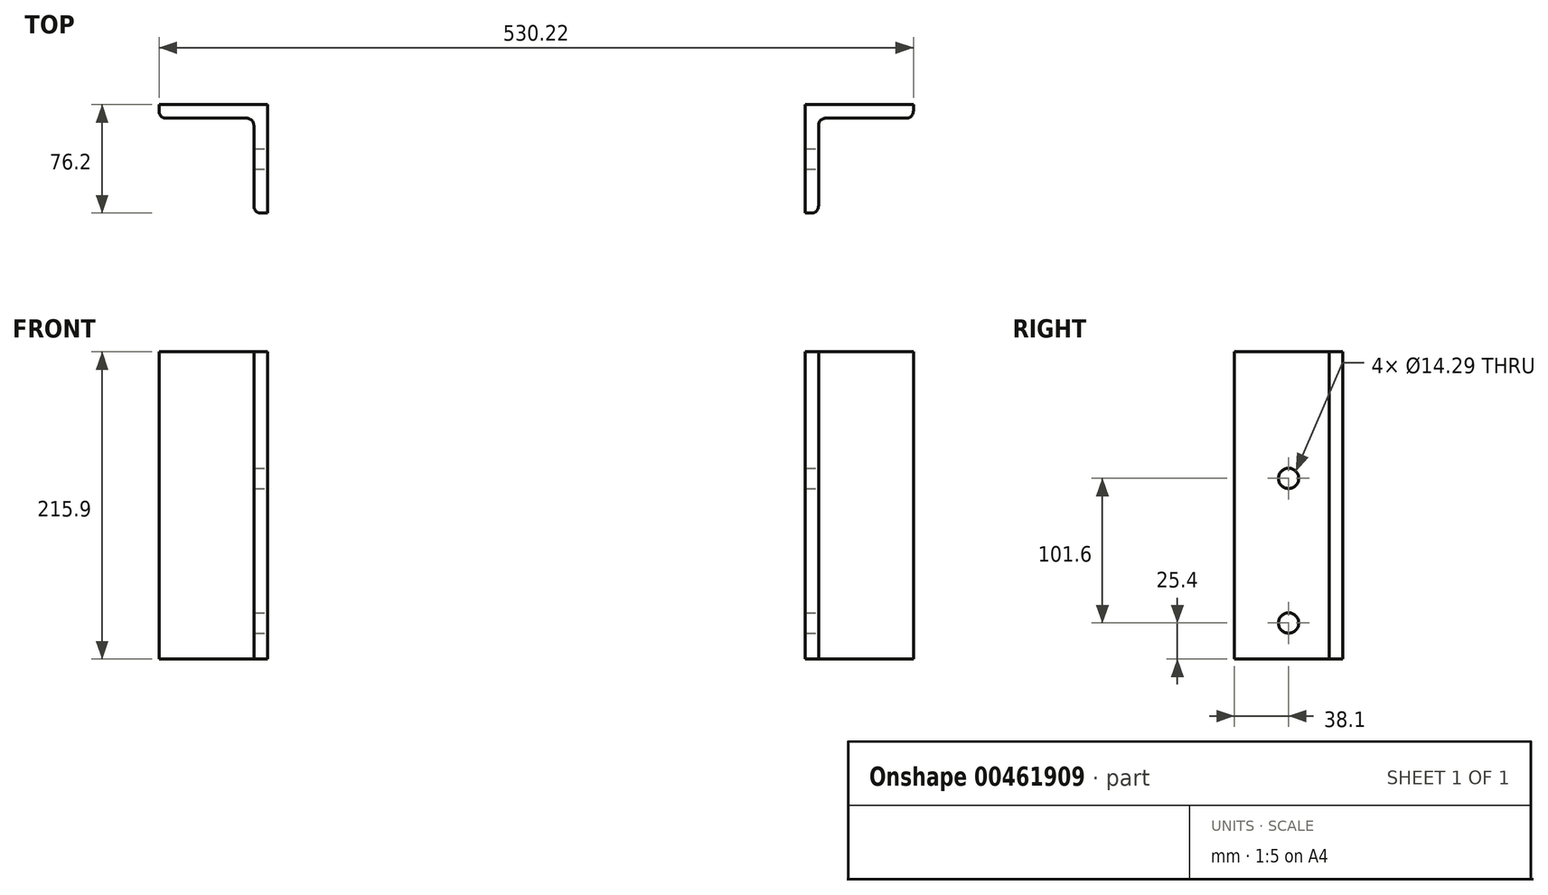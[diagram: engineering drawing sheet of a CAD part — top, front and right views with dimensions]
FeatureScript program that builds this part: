
annotation { "Feature Type Name" : "Feature", "Feature Type Description" : "" }
export const myFeature = defineFeature(function(context is Context, id is Id, definition is map)
    precondition{}
    {
        {
            var Q0;
            Q0=qCreatedBy(makeId("Top.planeOp"),FACE);
            var sketch = newSketch(context, id + "F0", { "sketchPlane" : qUnion([Q0])});
            skLineSegment(sketch, "E0.bottom", {"start": v(303.76, -38.1) * mm, "end": v(294.23, -38.1) * mm});
            skLineSegment(sketch, "E0.top", {"start": v(370.43, 38.1) * mm, "end": v(294.23, 38.1) * mm});
            skLineSegment(sketch, "E0.left", {"start": v(370.43, 28.58) * mm, "end": v(370.43, 38.1) * mm});
            skLineSegment(sketch, "E0.right", {"start": v(294.23, -38.1) * mm, "end": v(294.23, 38.1) * mm});
            skPoint(sketch, "E0.middle", {"position": v(332.33, 0) * mm});
            skLineSegment(sketch, "E1.bottom", {"start": v(-83.6, -38.1) * mm, "end": v(-93.12, -38.1) * mm});
            skLineSegment(sketch, "E1.top", {"start": v(-83.6, 38.1) * mm, "end": v(-159.8, 38.1) * mm});
            skLineSegment(sketch, "E1.left", {"start": v(-83.6, -38.1) * mm, "end": v(-83.6, 38.1) * mm});
            skLineSegment(sketch, "E1.right", {"start": v(-159.8, 28.58) * mm, "end": v(-159.8, 38.1) * mm});
            skPoint(sketch, "E1.middle", {"position": v(-121.7, 0) * mm});
            skLineSegment(sketch, "E2.0", {"start": v(-93.12, 28.57) * mm, "end": v(-159.8, 28.57) * mm});
            skLineSegment(sketch, "E3.0", {"start": v(-93.12, -38.1) * mm, "end": v(-93.12, 28.58) * mm});
            skLineSegment(sketch, "E4.0", {"start": v(370.43, 28.58) * mm, "end": v(303.76, 28.57) * mm});
            skLineSegment(sketch, "E5.0", {"start": v(303.76, -38.1) * mm, "end": v(303.76, 28.58) * mm});
            skPoint(sketch, "E6.orphan", {"position": v(370.43, -38.1) * mm});
            skPoint(sketch, "E7.orphan", {"position": v(-159.8, -38.1) * mm});
            skSolve(sketch);
        }
        {
            var Q0;
            Q0 = qSketchRegion(id + "F0", true);
            extrude(context, id + "F1", {"entities" : qUnion([Q0]), "endBound" : BoundingType.SYMMETRIC, "depth" : 215.9 * mm});
        }
        {
            var Q0;
            Q0=makeQuery(id+"F1.opExtrude","SWEPT_EDGE",EDGE,{"disambiguationData":[OSD([sQuery(id+"F0.wireOp",EDGE,"E1.right"),sQuery(id+"F0.wireOp",EDGE,"E2.0")])]});
            var Q1;
            Q1=makeQuery(id+"F1.opExtrude","SWEPT_EDGE",EDGE,{"disambiguationData":[OSD([sQuery(id+"F0.wireOp",EDGE,"E2.0"),sQuery(id+"F0.wireOp",EDGE,"E3.0")])]});
            var Q2;
            Q2=makeQuery(id+"F1.opExtrude","SWEPT_EDGE",EDGE,{"disambiguationData":[OSD([sQuery(id+"F0.wireOp",EDGE,"E1.bottom"),sQuery(id+"F0.wireOp",EDGE,"E3.0")])]});
            var Q3;
            Q3=makeQuery(id+"F1.opExtrude","SWEPT_EDGE",EDGE,{"disambiguationData":[OSD([sQuery(id+"F0.wireOp",EDGE,"E0.bottom"),sQuery(id+"F0.wireOp",EDGE,"E5.0")])]});
            var Q4;
            Q4=makeQuery(id+"F1.opExtrude","SWEPT_EDGE",EDGE,{"disambiguationData":[OSD([sQuery(id+"F0.wireOp",EDGE,"E4.0"),sQuery(id+"F0.wireOp",EDGE,"E5.0")])]});
            var Q5;
            Q5=makeQuery(id+"F1.opExtrude","SWEPT_EDGE",EDGE,{"disambiguationData":[OSD([sQuery(id+"F0.wireOp",EDGE,"E0.left"),sQuery(id+"F0.wireOp",EDGE,"E4.0")])]});
            fillet(context, id + "F2", {"entities" : qUnion([Q0, Q1, Q2, Q3, Q4, Q5]), "radius" : 5.08 * mm, "tangentPropagation" : true, "allowEdgeOverflow" : false});
        }
        {
            var Q0;
            Q0=makeQuery(id+"F1.opExtrude","SWEPT_FACE",FACE,{"disambiguationData":[OSD([sQuery(id+"F0.wireOp",EDGE,"E5.0")])]});
            var sketch = newSketch(context, id + "F3", { "sketchPlane" : qUnion([Q0])});
            skCircle(sketch, "E8", {"center": v(0, -82.55) * mm, "radius": 7.14 * mm});
            skCircle(sketch, "E9", {"center": v(0, 19.05) * mm, "radius": 7.14 * mm});
            skSolve(sketch);
        }
        {
            var Q0;
            Q0 = qSketchRegion(id + "F3", true);
            extrude(context, id + "F4", {"entities" : qUnion([Q0]), "operationType" : NewBodyOperationType.REMOVE, "endBound" : BoundingType.SYMMETRIC, "oppositeDirection" : true, "depth" : 817.88 * mm});
        }
        {
            var Q0;
            Q0=makeQuery(id+"F1.opExtrude","SWEPT_FACE",FACE,{"disambiguationData":[OSD([sQuery(id+"F0.wireOp",EDGE,"E1.left")])]});
            var sketch = newSketch(context, id + "F5", { "sketchPlane" : qUnion([Q0])});
            skCircle(sketch, "E10", {"center": v(0, -82.55) * mm, "radius": 7.14 * mm});
            skCircle(sketch, "E11", {"center": v(0, 19.05) * mm, "radius": 7.14 * mm});
            skSolve(sketch);
        }
        {
            var Q0;
            Q0 = qSketchRegion(id + "F5", true);
            extrude(context, id + "F6", {"entities" : qUnion([Q0]), "operationType" : NewBodyOperationType.REMOVE, "oppositeDirection" : true, "depth" : 25.4 * mm});
        }
    });
